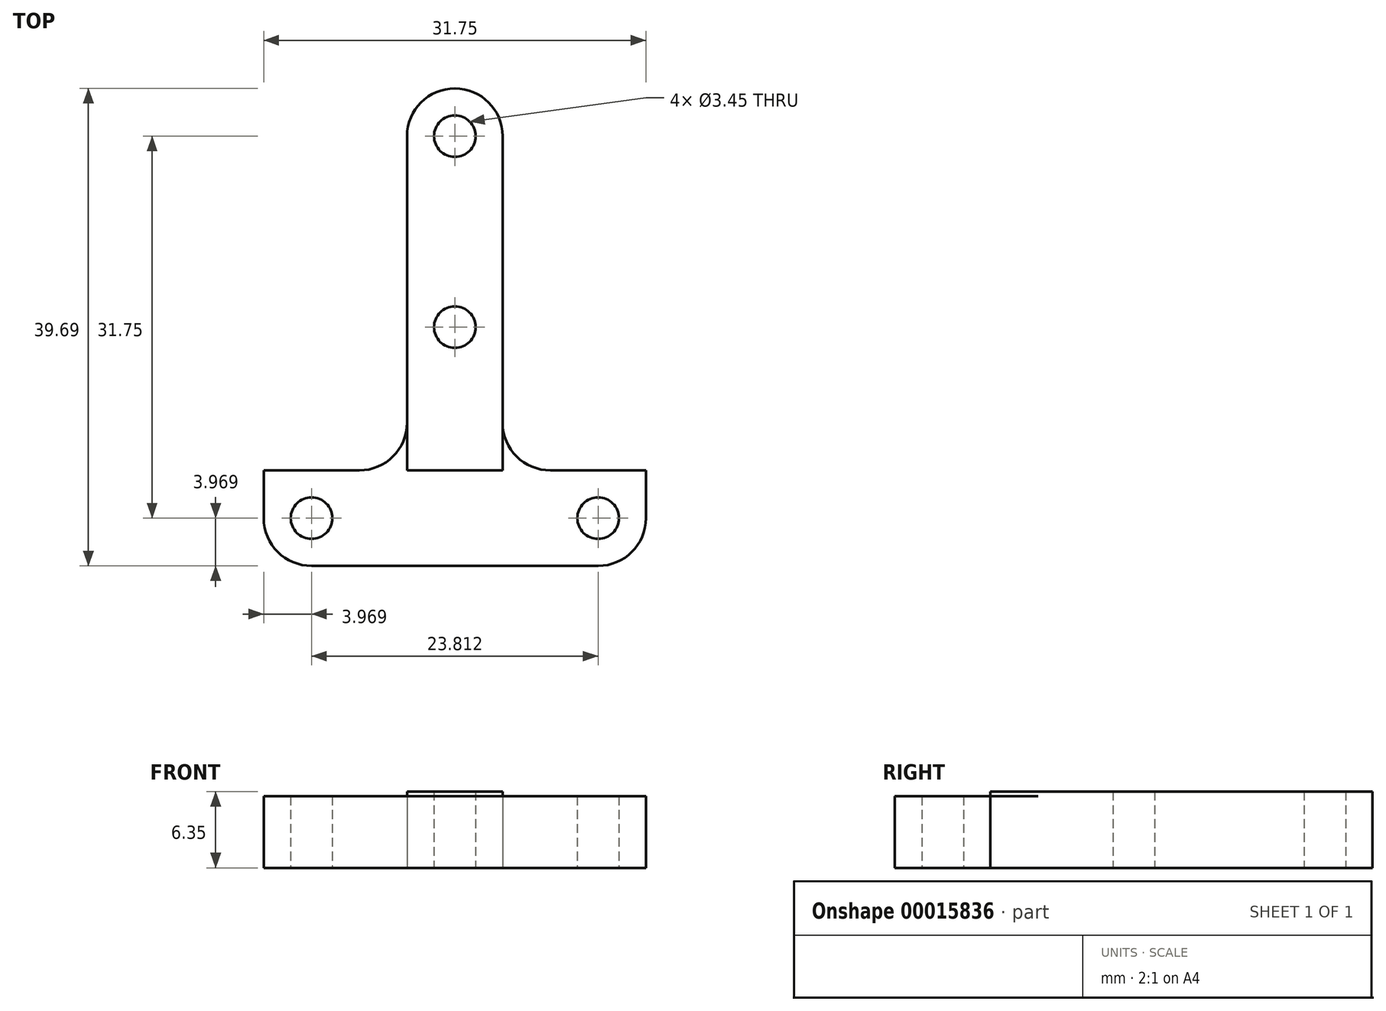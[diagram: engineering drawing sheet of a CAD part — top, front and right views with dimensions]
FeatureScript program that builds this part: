
annotation { "Feature Type Name" : "Feature", "Feature Type Description" : "" }
export const myFeature = defineFeature(function(context is Context, id is Id, definition is map)
    precondition{}
    {
        {
            var Q0;
            Q0=qCreatedBy(makeId("Top.planeOp"),FACE);
            var sketch = newSketch(context, id + "F0", { "sketchPlane" : qUnion([Q0])});
            skLineSegment(sketch, "E0.bottom", {"start": v(0, 0) * mm, "end": v(31.75, 0) * mm});
            skLineSegment(sketch, "E0.left", {"start": v(0, 0) * mm, "end": v(0, 7.94) * mm});
            skLineSegment(sketch, "E0.right", {"start": v(31.75, 0) * mm, "end": v(31.75, 7.94) * mm});
            skLineSegment(sketch, "E1", {"start": v(0, 7.94) * mm, "end": v(11.9, 7.94) * mm});
            skLineSegment(sketch, "E2", {"start": v(11.9, 7.94) * mm, "end": v(11.9, 39.69) * mm});
            skLineSegment(sketch, "E3", {"start": v(31.75, 7.94) * mm, "end": v(19.84, 7.94) * mm});
            skLineSegment(sketch, "E4", {"start": v(19.84, 7.94) * mm, "end": v(19.84, 39.69) * mm});
            skLineSegment(sketch, "E5", {"start": v(19.84, 39.69) * mm, "end": v(11.9, 39.69) * mm});
            skLineSegment(sketch, "E6", {"start": v(15.88, 39.69) * mm, "end": v(15.88, 35.72) * mm, "construction": true});
            skLineSegment(sketch, "E7", {"start": v(15.88, 35.72) * mm, "end": v(15.88, 19.84) * mm});
            skLineSegment(sketch, "E8", {"start": v(0, 3.97) * mm, "end": v(3.97, 3.97) * mm, "construction": true});
            skLineSegment(sketch, "E9", {"start": v(31.75, 3.97) * mm, "end": v(27.78, 3.97) * mm, "construction": true});
            skCircle(sketch, "E10", {"center": v(15.87, 35.72) * mm, "radius": 1.73 * mm});
            skCircle(sketch, "E11", {"center": v(15.87, 19.84) * mm, "radius": 1.73 * mm});
            skCircle(sketch, "E12", {"center": v(3.97, 3.97) * mm, "radius": 1.73 * mm});
            skCircle(sketch, "E13", {"center": v(27.78, 3.97) * mm, "radius": 1.73 * mm});
            skSolve(sketch);
        }
        {
            var Q0;
            Q0 = qSketchRegion(id + "F0", true);
            extrude(context, id + "F1", {"entities" : qUnion([Q0]), "depth" : 6.35 * mm});
        }
        {
            var Q0;
            Q0=makeQuery(id+"F1.opExtrude","SWEPT_EDGE",EDGE,{"disambiguationData":[OSD([sQuery(id+"F0.wireOp",EDGE,"E4"),sQuery(id+"F0.wireOp",EDGE,"E5")])]});
            var Q1;
            Q1=makeQuery(id+"F1.opExtrude","SWEPT_EDGE",EDGE,{"disambiguationData":[OSD([sQuery(id+"F0.wireOp",EDGE,"E2"),sQuery(id+"F0.wireOp",EDGE,"E5")])]});
            var Q2;
            Q2=makeQuery(id+"F1.opExtrude","SWEPT_EDGE",EDGE,{"disambiguationData":[OSD([sQuery(id+"F0.wireOp",EDGE,"E3"),sQuery(id+"F0.wireOp",EDGE,"E4")])]});
            var Q3;
            Q3=makeQuery(id+"F1.opExtrude","SWEPT_EDGE",EDGE,{"disambiguationData":[OSD([sQuery(id+"F0.wireOp",EDGE,"E1"),sQuery(id+"F0.wireOp",EDGE,"E2")])]});
            var Q4;
            Q4=makeQuery(id+"F1.opExtrude","SWEPT_EDGE",EDGE,{"disambiguationData":[OSD([sQuery(id+"F0.wireOp",EDGE,"E0.bottom"),sQuery(id+"F0.wireOp",EDGE,"E0.left")])]});
            var Q5;
            Q5=makeQuery(id+"F1.opExtrude","SWEPT_EDGE",EDGE,{"disambiguationData":[OSD([sQuery(id+"F0.wireOp",EDGE,"E0.bottom"),sQuery(id+"F0.wireOp",EDGE,"E0.right")])]});
            fillet(context, id + "F2", {"entities" : qUnion([Q0, Q1, Q2, Q3, Q4, Q5]), "radius" : 3.97 * mm, "tangentPropagation" : true, "allowEdgeOverflow" : false});
        }
        {
            var Q0;
            Q0=makeQuery(id+"F1.opExtrude","CAP_FACE",FACE,{"disambiguationData":[OSD([sQuery(id+"F0.wireOp",EDGE,"E0.bottom"),sQuery(id+"F0.wireOp",EDGE,"E0.left"),sQuery(id+"F0.wireOp",EDGE,"E0.right"),sQuery(id+"F0.wireOp",EDGE,"E1"),sQuery(id+"F0.wireOp",EDGE,"E2"),sQuery(id+"F0.wireOp",EDGE,"E3"),sQuery(id+"F0.wireOp",EDGE,"E4"),sQuery(id+"F0.wireOp",EDGE,"E5"),sQuery(id+"F0.wireOp",EDGE,"E10"),sQuery(id+"F0.wireOp",EDGE,"E11"),sQuery(id+"F0.wireOp",EDGE,"E12"),sQuery(id+"F0.wireOp",EDGE,"E13")])],"isStart":false});
            var sketch = newSketch(context, id + "F3", { "sketchPlane" : qUnion([Q0])});
            skLineSegment(sketch, "E14.bottom", {"start": v(0, 0) * mm, "end": v(31.75, 0) * mm});
            skLineSegment(sketch, "E14.top", {"start": v(0, 7.94) * mm, "end": v(31.75, 7.94) * mm});
            skLineSegment(sketch, "E14.left", {"start": v(0, 0) * mm, "end": v(0, 7.94) * mm});
            skLineSegment(sketch, "E14.right", {"start": v(31.75, 0) * mm, "end": v(31.75, 7.94) * mm});
            skLineSegment(sketch, "E15.bottom", {"start": v(11.9, 11.9) * mm, "end": v(7.94, 11.9) * mm});
            skLineSegment(sketch, "E15.top", {"start": v(11.9, 7.94) * mm, "end": v(7.94, 7.94) * mm});
            skLineSegment(sketch, "E15.left", {"start": v(11.9, 11.9) * mm, "end": v(11.9, 7.94) * mm});
            skLineSegment(sketch, "E15.right", {"start": v(7.94, 11.9) * mm, "end": v(7.94, 7.94) * mm});
            skLineSegment(sketch, "E16.bottom", {"start": v(19.84, 11.9) * mm, "end": v(23.81, 11.9) * mm});
            skLineSegment(sketch, "E16.top", {"start": v(19.84, 7.94) * mm, "end": v(23.81, 7.94) * mm});
            skLineSegment(sketch, "E16.left", {"start": v(19.84, 11.9) * mm, "end": v(19.84, 7.94) * mm});
            skLineSegment(sketch, "E16.right", {"start": v(23.81, 11.9) * mm, "end": v(23.81, 7.94) * mm});
            skSolve(sketch);
        }
        {
            var Q0;
            Q0 = qSketchRegion(id + "F3", true);
            extrude(context, id + "F4", {"entities" : qUnion([Q0]), "operationType" : NewBodyOperationType.REMOVE, "oppositeDirection" : true, "depth" : 0.4 * mm});
        }
    });
